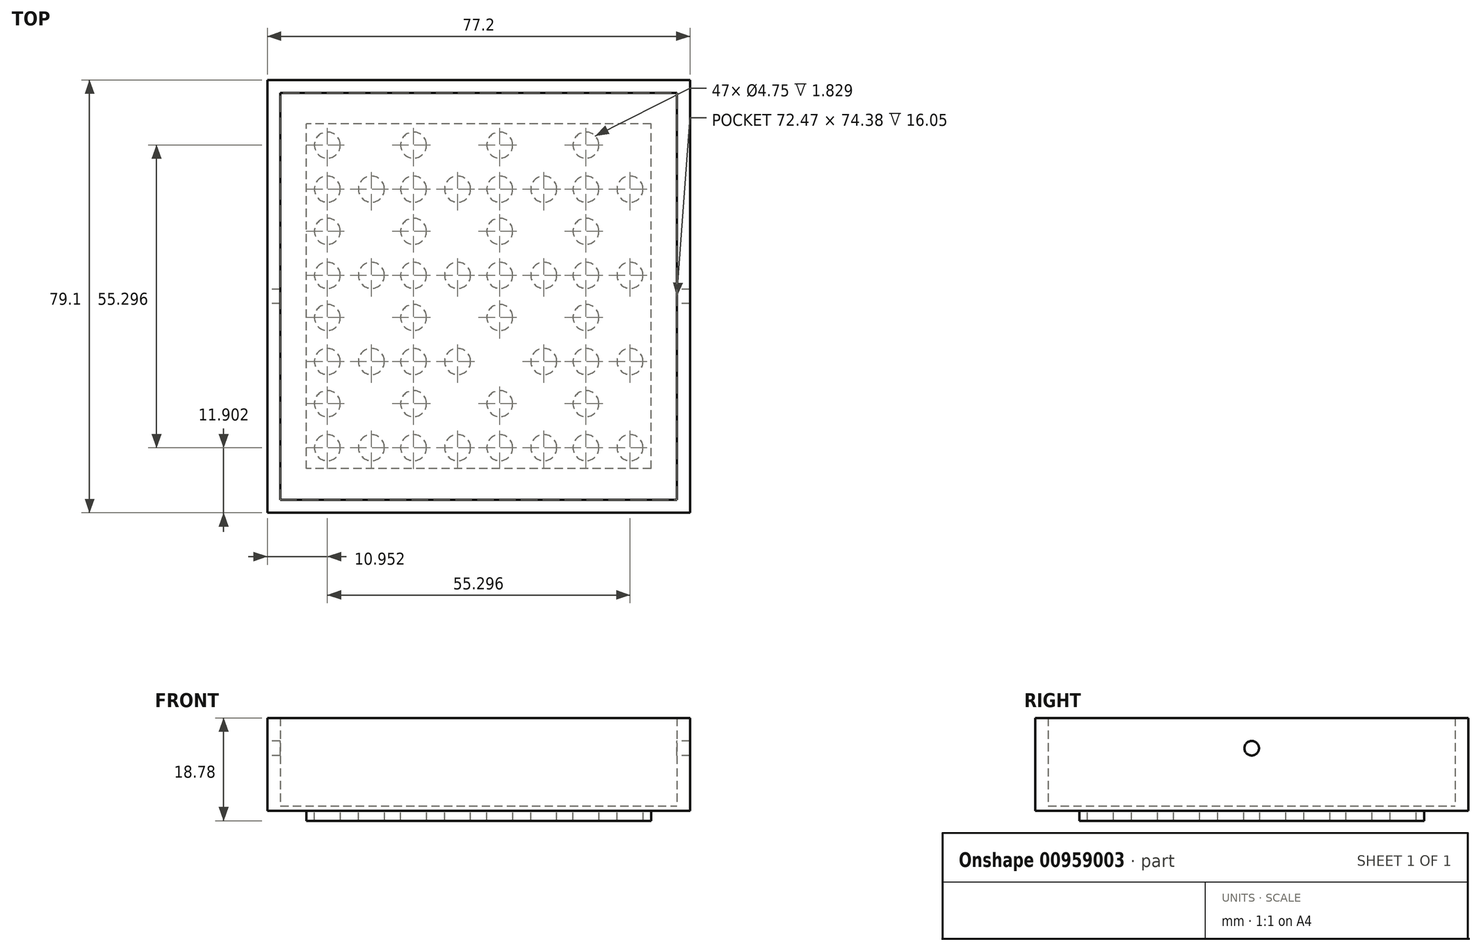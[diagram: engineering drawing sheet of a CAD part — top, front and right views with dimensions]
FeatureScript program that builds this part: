
annotation { "Feature Type Name" : "Feature", "Feature Type Description" : "" }
export const myFeature = defineFeature(function(context is Context, id is Id, definition is map)
    precondition{}
    {
        {
            var Q0;
            Q0=qCreatedBy(makeId("Top.planeOp"),FACE);
            var sketch = newSketch(context, id + "F0", { "sketchPlane" : qUnion([Q0])});
            skLineSegment(sketch, "E0.bottom", {"start": v(36.24, 37.19) * mm, "end": v(-36.24, 37.19) * mm});
            skLineSegment(sketch, "E0.top", {"start": v(36.24, -37.19) * mm, "end": v(-36.24, -37.19) * mm});
            skLineSegment(sketch, "E0.left", {"start": v(36.24, 37.19) * mm, "end": v(36.24, -37.19) * mm});
            skLineSegment(sketch, "E0.right", {"start": v(-36.24, 37.19) * mm, "end": v(-36.24, -37.19) * mm});
            skPoint(sketch, "E0.middle", {"position": v(0, 0) * mm});
            skLineSegment(sketch, "E1.bottom", {"start": v(-38.6, 39.55) * mm, "end": v(38.6, 39.55) * mm});
            skLineSegment(sketch, "E1.top", {"start": v(-38.6, -39.55) * mm, "end": v(38.6, -39.55) * mm});
            skLineSegment(sketch, "E1.left", {"start": v(-38.6, 39.55) * mm, "end": v(-38.6, -39.55) * mm});
            skLineSegment(sketch, "E1.right", {"start": v(38.6, 39.55) * mm, "end": v(38.6, -39.55) * mm});
            skSolve(sketch);
        }
        {
            var Q0;
            Q0=makeQuery(id+"F0.imprint","IMPRINT",FACE,{"disambiguationData":[TD([[makeQuery(id+"F0.imprint","IMPRINT",EDGE,{"derivedFrom":sQuery(id+"F0.wireOp",EDGE,"E0.bottom")}),-1.0]])]});
            extrude(context, id + "F1", {"entities" : qUnion([Q0]), "depth" : 16.95 * mm, "offsetDistance" : 25.4 * mm});
        }
        {
            var Q0;
            Q0=makeQuery(id+"F1.opExtrude","SWEPT_FACE",FACE,{"disambiguationData":[OSD([sQuery(id+"F0.wireOp",EDGE,"E1.left")])]});
            var sketch = newSketch(context, id + "F2", { "sketchPlane" : qUnion([Q0])});
            skLineSegment(sketch, "E2", {"start": v(-39.55, 0.9) * mm, "end": v(39.55, 0.9) * mm});
            skSolve(sketch);
        }
        {
            var Q0;
            {var subQ0=sQuery(id+"F2.wireOp",EDGE,"E2");Q0=makeQuery(id+"F2.imprint","IMPRINT",FACE,{"disambiguationData":[TD([[makeQuery(id+"F2.imprint","IMPRINT",EDGE,{"derivedFrom":subQ0}),-1.0]])]});}
            var Q1;
            Q1=makeQuery(id+"F1.opExtrude","SWEPT_FACE",FACE,{"disambiguationData":[OSD([sQuery(id+"F0.wireOp",EDGE,"E0.left")])]});
            extrude(context, id + "F3", {"entities" : qUnion([Q0]), "operationType" : NewBodyOperationType.ADD, "endBound" : BoundingType.UP_TO_SURFACE, "oppositeDirection" : true, "depth" : 25.4 * mm, "endBoundEntityFace" : qUnion([Q1]), "offsetDistance" : 25.4 * mm});
        }
        {
            var Q0;
            Q0=makeQuery(id+"F1.opExtrude","SWEPT_FACE",FACE,{"disambiguationData":[OSD([sQuery(id+"F0.wireOp",EDGE,"E1.left")])]});
            var sketch = newSketch(context, id + "F4", { "sketchPlane" : qUnion([Q0])});
            skLineSegment(sketch, "E3", {"start": v(39.55, 5.9) * mm, "end": v(-39.55, 5.9) * mm, "construction": true});
            skLineSegment(sketch, "E4", {"start": v(-39.55, 11.42) * mm, "end": v(39.55, 11.42) * mm, "construction": true});
            skCircle(sketch, "E5", {"center": v(0, 11.42) * mm, "radius": 1.33 * mm});
            skSolve(sketch);
        }
        {
            var Q0;
            Q0=makeQuery(id+"F4.imprint","IMPRINT",FACE,{"disambiguationData":[TD([[makeQuery(id+"F4.imprint","IMPRINT",EDGE,{"derivedFrom":sQuery(id+"F4.wireOp",EDGE,"E5")}),1.0]])]});
            extrude(context, id + "F5", {"entities" : qUnion([Q0]), "operationType" : NewBodyOperationType.REMOVE, "endBound" : BoundingType.THROUGH_ALL, "oppositeDirection" : true, "depth" : 25.4 * mm, "offsetDistance" : 25.4 * mm});
        }
        {
            var Q0;
            {var subQ0=sQuery(id+"F0.wireOp",EDGE,"E1.left");Q0=makeQuery(id+"F3.boolean.opBoolean","MERGE",FACE,{"derivedFrom":[makeQuery(id+"F1.opExtrude","CAP_FACE",FACE,{"disambiguationData":[OSD([sQuery(id+"F0.wireOp",EDGE,"E0.bottom"),sQuery(id+"F0.wireOp",EDGE,"E0.top"),sQuery(id+"F0.wireOp",EDGE,"E0.left"),sQuery(id+"F0.wireOp",EDGE,"E0.right"),sQuery(id+"F0.wireOp",EDGE,"E1.bottom"),sQuery(id+"F0.wireOp",EDGE,"E1.top"),subQ0,sQuery(id+"F0.wireOp",EDGE,"E1.right")])],"isStart":true}),makeQuery(id+"F3.opExtrude","SWEPT_FACE",FACE,{"disambiguationData":[OSD([subQ0])]})]});}
            var sketch = newSketch(context, id + "F6", { "sketchPlane" : qUnion([Q0])});
            skLineSegment(sketch, "E6.bottom", {"start": v(15.75, 15.75) * mm, "end": v(0, 15.75) * mm});
            skLineSegment(sketch, "E6.top", {"start": v(15.75, 0) * mm, "end": v(0, 0) * mm});
            skLineSegment(sketch, "E6.left", {"start": v(15.75, 15.75) * mm, "end": v(15.75, 0) * mm});
            skLineSegment(sketch, "E6.right", {"start": v(0, 15.75) * mm, "end": v(0, 0) * mm});
            skPoint(sketch, "E6.middle", {"position": v(7.87, 7.87) * mm});
            skLineSegment(sketch, "E7.bottom", {"start": v(14.27, 14.27) * mm, "end": v(1.47, 14.27) * mm, "construction": true});
            skLineSegment(sketch, "E7.top", {"start": v(14.27, 1.47) * mm, "end": v(1.47, 1.47) * mm, "construction": true});
            skLineSegment(sketch, "E7.left", {"start": v(14.27, 14.27) * mm, "end": v(14.27, 1.47) * mm, "construction": true});
            skLineSegment(sketch, "E7.right", {"start": v(1.47, 14.27) * mm, "end": v(1.47, 1.47) * mm, "construction": true});
            skCircle(sketch, "E8", {"center": v(3.85, 11.9) * mm, "radius": 2.37 * mm});
            skLineSegment(sketch, "E9", {"start": v(7.87, 14.27) * mm, "end": v(7.87, 1.47) * mm, "construction": true});
            skLineSegment(sketch, "E10", {"start": v(1.47, 7.87) * mm, "end": v(14.27, 7.87) * mm, "construction": true});
            skLineSegment(sketch, "E11.MirrorCS", {"start": v(14.27, 7.87) * mm, "end": v(1.47, 7.87) * mm, "construction": true});
            skCircle(sketch, "E12.MirrorC", {"center": v(11.9, 11.9) * mm, "radius": 2.37 * mm});
            skCircle(sketch, "E13.MirrorC", {"center": v(3.85, 3.85) * mm, "radius": 2.37 * mm});
            skCircle(sketch, "E14.MirrorC", {"center": v(11.9, 3.85) * mm, "radius": 2.37 * mm});
            skLineSegment(sketch, "E15.0.1.1", {"start": v(14.27, 30.02) * mm, "end": v(14.27, 17.22) * mm, "construction": true});
            skLineSegment(sketch, "E15.0.1.2", {"start": v(7.87, 30.02) * mm, "end": v(7.87, 17.22) * mm, "construction": true});
            skCircle(sketch, "E15.0.1.3", {"center": v(11.9, 19.6) * mm, "radius": 2.37 * mm});
            skCircle(sketch, "E15.0.1.4", {"center": v(3.85, 27.65) * mm, "radius": 2.37 * mm});
            skCircle(sketch, "E15.0.1.5", {"center": v(3.85, 19.6) * mm, "radius": 2.37 * mm});
            skLineSegment(sketch, "E15.0.1.6", {"start": v(1.47, 23.62) * mm, "end": v(14.27, 23.62) * mm, "construction": true});
            skLineSegment(sketch, "E15.0.1.7", {"start": v(14.27, 30.02) * mm, "end": v(1.47, 30.02) * mm, "construction": true});
            skCircle(sketch, "E15.0.1.8", {"center": v(11.9, 27.65) * mm, "radius": 2.37 * mm});
            skLineSegment(sketch, "E15.0.1.9", {"start": v(14.27, 17.22) * mm, "end": v(1.47, 17.22) * mm, "construction": true});
            skPoint(sketch, "E15.0.1.10", {"position": v(7.87, 23.62) * mm});
            skLineSegment(sketch, "E15.0.1.11", {"start": v(15.75, 31.5) * mm, "end": v(15.75, 15.75) * mm});
            skLineSegment(sketch, "E15.0.1.12", {"start": v(15.75, 31.5) * mm, "end": v(0, 31.5) * mm});
            skLineSegment(sketch, "E15.0.1.13", {"start": v(0, 31.5) * mm, "end": v(0, 15.75) * mm});
            skLineSegment(sketch, "E15.0.1.14", {"start": v(1.47, 30.02) * mm, "end": v(1.47, 17.22) * mm, "construction": true});
            skPoint(sketch, "E15.0.1.15", {"position": v(7.87, 23.62) * mm});
            skLineSegment(sketch, "E15.0.1.16", {"start": v(14.27, 23.62) * mm, "end": v(1.47, 23.62) * mm, "construction": true});
            skCircle(sketch, "E15.0.1.17", {"center": v(3.85, 27.65) * mm, "radius": 2.37 * mm});
            skLineSegment(sketch, "E15.0.1.18", {"start": v(1.47, 23.62) * mm, "end": v(14.27, 23.62) * mm, "construction": true});
            skLineSegment(sketch, "E15.1.0.0", {"start": v(31.5, 0) * mm, "end": v(15.75, 0) * mm});
            skLineSegment(sketch, "E15.1.0.1", {"start": v(30.02, 14.27) * mm, "end": v(30.02, 1.47) * mm, "construction": true});
            skLineSegment(sketch, "E15.1.0.2", {"start": v(23.62, 14.27) * mm, "end": v(23.62, 1.47) * mm, "construction": true});
            skCircle(sketch, "E15.1.0.3", {"center": v(27.65, 3.85) * mm, "radius": 2.37 * mm});
            skCircle(sketch, "E15.1.0.4", {"center": v(19.6, 11.9) * mm, "radius": 2.37 * mm});
            skCircle(sketch, "E15.1.0.5", {"center": v(19.6, 3.85) * mm, "radius": 2.37 * mm});
            skLineSegment(sketch, "E15.1.0.6", {"start": v(17.22, 7.87) * mm, "end": v(30.02, 7.87) * mm, "construction": true});
            skLineSegment(sketch, "E15.1.0.7", {"start": v(30.02, 14.27) * mm, "end": v(17.22, 14.27) * mm, "construction": true});
            skCircle(sketch, "E15.1.0.8", {"center": v(27.65, 11.9) * mm, "radius": 2.37 * mm});
            skLineSegment(sketch, "E15.1.0.9", {"start": v(30.02, 1.47) * mm, "end": v(17.22, 1.47) * mm, "construction": true});
            skPoint(sketch, "E15.1.0.10", {"position": v(23.62, 7.87) * mm});
            skLineSegment(sketch, "E15.1.0.11", {"start": v(31.5, 15.75) * mm, "end": v(31.5, 0) * mm});
            skLineSegment(sketch, "E15.1.0.12", {"start": v(31.5, 15.75) * mm, "end": v(15.75, 15.75) * mm});
            skLineSegment(sketch, "E15.1.0.14", {"start": v(17.22, 14.27) * mm, "end": v(17.22, 1.47) * mm, "construction": true});
            skPoint(sketch, "E15.1.0.15", {"position": v(23.62, 7.87) * mm});
            skLineSegment(sketch, "E15.1.0.16", {"start": v(30.02, 7.87) * mm, "end": v(17.22, 7.87) * mm, "construction": true});
            skCircle(sketch, "E15.1.0.17", {"center": v(19.6, 11.9) * mm, "radius": 2.37 * mm});
            skLineSegment(sketch, "E15.1.0.18", {"start": v(17.22, 7.87) * mm, "end": v(30.02, 7.87) * mm, "construction": true});
            skLineSegment(sketch, "E15.1.1.0", {"start": v(31.5, 15.75) * mm, "end": v(15.75, 15.75) * mm});
            skLineSegment(sketch, "E15.1.1.1", {"start": v(30.02, 30.02) * mm, "end": v(30.02, 17.22) * mm, "construction": true});
            skLineSegment(sketch, "E15.1.1.2", {"start": v(23.62, 30.02) * mm, "end": v(23.62, 17.22) * mm, "construction": true});
            skCircle(sketch, "E15.1.1.3", {"center": v(27.65, 19.6) * mm, "radius": 2.37 * mm});
            skCircle(sketch, "E15.1.1.4", {"center": v(19.6, 27.65) * mm, "radius": 2.37 * mm});
            skCircle(sketch, "E15.1.1.5", {"center": v(19.6, 19.6) * mm, "radius": 2.37 * mm});
            skLineSegment(sketch, "E15.1.1.6", {"start": v(17.22, 23.62) * mm, "end": v(30.02, 23.62) * mm, "construction": true});
            skLineSegment(sketch, "E15.1.1.7", {"start": v(30.02, 30.02) * mm, "end": v(17.22, 30.02) * mm, "construction": true});
            skCircle(sketch, "E15.1.1.8", {"center": v(27.65, 27.65) * mm, "radius": 2.37 * mm});
            skLineSegment(sketch, "E15.1.1.9", {"start": v(30.02, 17.22) * mm, "end": v(17.22, 17.22) * mm, "construction": true});
            skPoint(sketch, "E15.1.1.10", {"position": v(23.62, 23.62) * mm});
            skLineSegment(sketch, "E15.1.1.11", {"start": v(31.5, 31.5) * mm, "end": v(31.5, 15.75) * mm});
            skLineSegment(sketch, "E15.1.1.12", {"start": v(31.5, 31.5) * mm, "end": v(15.75, 31.5) * mm});
            skLineSegment(sketch, "E15.1.1.13", {"start": v(15.75, 31.5) * mm, "end": v(15.75, 15.75) * mm});
            skLineSegment(sketch, "E15.1.1.14", {"start": v(17.22, 30.02) * mm, "end": v(17.22, 17.22) * mm, "construction": true});
            skPoint(sketch, "E15.1.1.15", {"position": v(23.62, 23.62) * mm});
            skLineSegment(sketch, "E15.1.1.16", {"start": v(30.02, 23.62) * mm, "end": v(17.22, 23.62) * mm, "construction": true});
            skCircle(sketch, "E15.1.1.17", {"center": v(19.6, 27.65) * mm, "radius": 2.37 * mm});
            skLineSegment(sketch, "E15.1.1.18", {"start": v(17.22, 23.62) * mm, "end": v(30.02, 23.62) * mm, "construction": true});
            skLineSegment(sketch, "E15.direction1", {"start": v(0, 0) * mm, "end": v(15.75, 0) * mm, "construction": true});
            skLineSegment(sketch, "E15.direction2", {"start": v(0, 0) * mm, "end": v(0, 15.75) * mm, "construction": true});
            skPoint(sketch, "E16.0.1.0", {"position": v(23.62, -7.87) * mm});
            skLineSegment(sketch, "E16.0.1.1", {"start": v(1.47, -17.22) * mm, "end": v(1.47, -30.02) * mm, "construction": true});
            skLineSegment(sketch, "E16.0.1.3", {"start": v(14.27, -17.22) * mm, "end": v(14.27, -30.02) * mm, "construction": true});
            skLineSegment(sketch, "E16.0.1.4", {"start": v(17.22, -23.62) * mm, "end": v(30.02, -23.62) * mm, "construction": true});
            skLineSegment(sketch, "E16.0.1.5", {"start": v(31.5, -15.75) * mm, "end": v(15.75, -15.75) * mm});
            skLineSegment(sketch, "E16.0.1.6", {"start": v(17.22, -7.87) * mm, "end": v(30.02, -7.87) * mm, "construction": true});
            skCircle(sketch, "E16.0.1.7", {"center": v(11.9, -19.6) * mm, "radius": 2.37 * mm});
            skCircle(sketch, "E16.0.1.8", {"center": v(27.65, -19.6) * mm, "radius": 2.37 * mm});
            skCircle(sketch, "E16.0.1.9", {"center": v(19.6, -11.9) * mm, "radius": 2.37 * mm});
            skLineSegment(sketch, "E16.0.1.10", {"start": v(1.47, -1.47) * mm, "end": v(1.47, -14.27) * mm, "construction": true});
            skLineSegment(sketch, "E16.0.1.11", {"start": v(30.02, -1.47) * mm, "end": v(30.02, -14.27) * mm, "construction": true});
            skLineSegment(sketch, "E16.0.1.12", {"start": v(31.5, -15.75) * mm, "end": v(31.5, -31.5) * mm});
            skCircle(sketch, "E16.0.1.13", {"center": v(3.85, -27.65) * mm, "radius": 2.37 * mm});
            skLineSegment(sketch, "E16.0.1.14", {"start": v(14.27, -30.02) * mm, "end": v(1.47, -30.02) * mm, "construction": true});
            skCircle(sketch, "E16.0.1.15", {"center": v(19.6, -3.85) * mm, "radius": 2.37 * mm});
            skCircle(sketch, "E16.0.1.16", {"center": v(19.6, -27.65) * mm, "radius": 2.37 * mm});
            skLineSegment(sketch, "E16.0.1.17", {"start": v(14.27, -17.22) * mm, "end": v(1.47, -17.22) * mm, "construction": true});
            skLineSegment(sketch, "E16.0.1.18", {"start": v(15.75, -15.75) * mm, "end": v(15.75, -31.5) * mm});
            skLineSegment(sketch, "E16.0.1.19", {"start": v(31.5, -31.5) * mm, "end": v(15.75, -31.5) * mm});
            skLineSegment(sketch, "E16.0.1.20", {"start": v(15.75, -15.75) * mm, "end": v(0, -15.75) * mm});
            skLineSegment(sketch, "E16.0.1.21", {"start": v(30.02, -1.47) * mm, "end": v(17.22, -1.47) * mm, "construction": true});
            skCircle(sketch, "E16.0.1.22", {"center": v(11.9, -3.85) * mm, "radius": 2.37 * mm});
            skLineSegment(sketch, "E16.0.1.23", {"start": v(23.62, -17.22) * mm, "end": v(23.62, -30.02) * mm, "construction": true});
            skLineSegment(sketch, "E16.0.1.24", {"start": v(31.5, 0) * mm, "end": v(31.5, -15.75) * mm});
            skCircle(sketch, "E16.0.1.25", {"center": v(27.65, -27.65) * mm, "radius": 2.37 * mm});
            skLineSegment(sketch, "E16.0.1.26", {"start": v(7.87, -1.47) * mm, "end": v(7.87, -14.27) * mm, "construction": true});
            skLineSegment(sketch, "E16.0.1.27", {"start": v(30.02, -17.22) * mm, "end": v(17.22, -17.22) * mm, "construction": true});
            skLineSegment(sketch, "E16.0.1.28", {"start": v(14.27, -1.47) * mm, "end": v(14.27, -14.27) * mm, "construction": true});
            skLineSegment(sketch, "E16.0.1.29", {"start": v(15.75, 0) * mm, "end": v(15.75, -15.75) * mm});
            skLineSegment(sketch, "E16.0.1.30", {"start": v(1.47, -7.87) * mm, "end": v(14.27, -7.87) * mm, "construction": true});
            skPoint(sketch, "E16.0.1.31", {"position": v(7.87, -7.87) * mm});
            skLineSegment(sketch, "E16.0.1.32", {"start": v(14.27, -14.27) * mm, "end": v(1.47, -14.27) * mm, "construction": true});
            skLineSegment(sketch, "E16.0.1.33", {"start": v(17.22, -17.22) * mm, "end": v(17.22, -30.02) * mm, "construction": true});
            skLineSegment(sketch, "E16.0.1.34", {"start": v(0, -31.5) * mm, "end": v(0, -15.75) * mm, "construction": true});
            skCircle(sketch, "E16.0.1.35", {"center": v(27.65, -11.9) * mm, "radius": 2.37 * mm});
            skCircle(sketch, "E16.0.1.36", {"center": v(11.9, -11.9) * mm, "radius": 2.37 * mm});
            skPoint(sketch, "E16.0.1.37", {"position": v(7.87, -23.62) * mm});
            skCircle(sketch, "E16.0.1.38", {"center": v(3.85, -19.6) * mm, "radius": 2.37 * mm});
            skLineSegment(sketch, "E16.0.1.39", {"start": v(0, 0) * mm, "end": v(0, -15.75) * mm});
            skLineSegment(sketch, "E16.0.1.40", {"start": v(30.02, -30.02) * mm, "end": v(17.22, -30.02) * mm, "construction": true});
            skLineSegment(sketch, "E16.0.1.41", {"start": v(17.22, -1.47) * mm, "end": v(17.22, -14.27) * mm, "construction": true});
            skCircle(sketch, "E16.0.1.42", {"center": v(27.65, -3.85) * mm, "radius": 2.37 * mm});
            skCircle(sketch, "E16.0.1.43", {"center": v(19.6, -19.6) * mm, "radius": 2.37 * mm});
            skCircle(sketch, "E16.0.1.44", {"center": v(3.85, -11.9) * mm, "radius": 2.37 * mm});
            skPoint(sketch, "E16.0.1.45", {"position": v(23.62, -23.62) * mm});
            skLineSegment(sketch, "E16.0.1.46", {"start": v(30.02, -14.27) * mm, "end": v(17.22, -14.27) * mm, "construction": true});
            skLineSegment(sketch, "E16.0.1.47", {"start": v(0, -31.5) * mm, "end": v(15.75, -31.5) * mm, "construction": true});
            skCircle(sketch, "E16.0.1.48", {"center": v(3.85, -3.85) * mm, "radius": 2.37 * mm});
            skLineSegment(sketch, "E16.0.1.49", {"start": v(14.27, -1.47) * mm, "end": v(1.47, -1.47) * mm, "construction": true});
            skLineSegment(sketch, "E16.0.1.50", {"start": v(30.02, -17.22) * mm, "end": v(30.02, -30.02) * mm, "construction": true});
            skCircle(sketch, "E16.0.1.51", {"center": v(11.9, -27.65) * mm, "radius": 2.37 * mm});
            skLineSegment(sketch, "E16.0.1.52", {"start": v(1.47, -23.62) * mm, "end": v(14.27, -23.62) * mm, "construction": true});
            skLineSegment(sketch, "E16.0.1.53", {"start": v(23.62, -1.47) * mm, "end": v(23.62, -14.27) * mm, "construction": true});
            skLineSegment(sketch, "E16.0.1.55", {"start": v(7.87, -17.22) * mm, "end": v(7.87, -30.02) * mm, "construction": true});
            skLineSegment(sketch, "E16.0.1.56", {"start": v(30.02, -7.87) * mm, "end": v(17.22, -7.87) * mm, "construction": true});
            skLineSegment(sketch, "E16.0.1.57", {"start": v(0, -15.75) * mm, "end": v(0, -31.5) * mm});
            skLineSegment(sketch, "E16.0.1.58", {"start": v(15.75, -31.5) * mm, "end": v(0, -31.5) * mm});
            skLineSegment(sketch, "E16.0.1.59", {"start": v(1.47, -7.87) * mm, "end": v(14.27, -7.87) * mm, "construction": true});
            skLineSegment(sketch, "E16.0.1.60", {"start": v(15.75, 0) * mm, "end": v(15.75, -15.75) * mm});
            skLineSegment(sketch, "E16.0.1.61", {"start": v(30.02, -23.62) * mm, "end": v(17.22, -23.62) * mm, "construction": true});
            skCircle(sketch, "E16.0.1.62", {"center": v(19.6, -3.85) * mm, "radius": 2.37 * mm});
            skLineSegment(sketch, "E16.0.1.63", {"start": v(31.5, -15.75) * mm, "end": v(15.75, -15.75) * mm});
            skCircle(sketch, "E16.0.1.64", {"center": v(3.85, -19.6) * mm, "radius": 2.37 * mm});
            skPoint(sketch, "E16.0.1.65", {"position": v(23.62, -23.62) * mm});
            skLineSegment(sketch, "E16.0.1.66", {"start": v(15.75, -15.75) * mm, "end": v(15.75, -31.5) * mm});
            skPoint(sketch, "E16.0.1.67", {"position": v(7.87, -23.62) * mm});
            skLineSegment(sketch, "E16.0.1.68", {"start": v(14.27, -23.62) * mm, "end": v(1.47, -23.62) * mm, "construction": true});
            skPoint(sketch, "E16.0.1.69", {"position": v(23.62, -7.87) * mm});
            skCircle(sketch, "E16.0.1.70", {"center": v(19.6, -19.6) * mm, "radius": 2.37 * mm});
            skPoint(sketch, "E16.0.1.71", {"position": v(7.87, -7.87) * mm});
            skLineSegment(sketch, "E16.0.1.72", {"start": v(15.75, -15.75) * mm, "end": v(0, -15.75) * mm});
            skCircle(sketch, "E16.0.1.73", {"center": v(3.85, -3.85) * mm, "radius": 2.37 * mm});
            skLineSegment(sketch, "E16.0.1.74", {"start": v(17.22, -7.87) * mm, "end": v(30.02, -7.87) * mm, "construction": true});
            skLineSegment(sketch, "E16.0.1.75", {"start": v(17.22, -23.62) * mm, "end": v(30.02, -23.62) * mm, "construction": true});
            skLineSegment(sketch, "E16.0.1.76", {"start": v(1.47, -23.62) * mm, "end": v(14.27, -23.62) * mm, "construction": true});
            skLineSegment(sketch, "E16.0.1.77", {"start": v(14.27, -7.87) * mm, "end": v(1.47, -7.87) * mm, "construction": true});
            skPoint(sketch, "E16.1.0.0", {"position": v(-7.87, 23.62) * mm});
            skLineSegment(sketch, "E16.1.0.1", {"start": v(-30.02, 14.27) * mm, "end": v(-30.02, 1.47) * mm, "construction": true});
            skLineSegment(sketch, "E16.1.0.2", {"start": v(-15.75, 31.5) * mm, "end": v(-31.5, 31.5) * mm});
            skLineSegment(sketch, "E16.1.0.3", {"start": v(-17.22, 14.27) * mm, "end": v(-17.22, 1.47) * mm, "construction": true});
            skLineSegment(sketch, "E16.1.0.4", {"start": v(-14.27, 7.87) * mm, "end": v(-1.47, 7.87) * mm, "construction": true});
            skLineSegment(sketch, "E16.1.0.5", {"start": v(0, 15.75) * mm, "end": v(-15.75, 15.75) * mm});
            skLineSegment(sketch, "E16.1.0.6", {"start": v(-14.27, 23.62) * mm, "end": v(-1.47, 23.62) * mm, "construction": true});
            skCircle(sketch, "E16.1.0.7", {"center": v(-19.6, 11.9) * mm, "radius": 2.37 * mm});
            skCircle(sketch, "E16.1.0.8", {"center": v(-3.85, 11.9) * mm, "radius": 2.37 * mm});
            skCircle(sketch, "E16.1.0.9", {"center": v(-11.9, 19.6) * mm, "radius": 2.37 * mm});
            skLineSegment(sketch, "E16.1.0.10", {"start": v(-30.02, 30.02) * mm, "end": v(-30.02, 17.22) * mm, "construction": true});
            skLineSegment(sketch, "E16.1.0.11", {"start": v(-1.47, 30.02) * mm, "end": v(-1.47, 17.22) * mm, "construction": true});
            skCircle(sketch, "E16.1.0.13", {"center": v(-27.65, 3.85) * mm, "radius": 2.37 * mm});
            skLineSegment(sketch, "E16.1.0.14", {"start": v(-17.22, 1.47) * mm, "end": v(-30.02, 1.47) * mm, "construction": true});
            skCircle(sketch, "E16.1.0.15", {"center": v(-11.9, 27.65) * mm, "radius": 2.37 * mm});
            skCircle(sketch, "E16.1.0.16", {"center": v(-11.9, 3.85) * mm, "radius": 2.37 * mm});
            skLineSegment(sketch, "E16.1.0.17", {"start": v(-17.22, 14.27) * mm, "end": v(-30.02, 14.27) * mm, "construction": true});
            skLineSegment(sketch, "E16.1.0.18", {"start": v(-15.75, 15.75) * mm, "end": v(-15.75, 0) * mm});
            skLineSegment(sketch, "E16.1.0.19", {"start": v(0, 0) * mm, "end": v(-15.75, 0) * mm});
            skLineSegment(sketch, "E16.1.0.20", {"start": v(-15.75, 15.75) * mm, "end": v(-31.5, 15.75) * mm});
            skLineSegment(sketch, "E16.1.0.21", {"start": v(-1.47, 30.02) * mm, "end": v(-14.27, 30.02) * mm, "construction": true});
            skCircle(sketch, "E16.1.0.22", {"center": v(-19.6, 27.65) * mm, "radius": 2.37 * mm});
            skLineSegment(sketch, "E16.1.0.23", {"start": v(-7.87, 14.27) * mm, "end": v(-7.87, 1.47) * mm, "construction": true});
            skCircle(sketch, "E16.1.0.25", {"center": v(-3.85, 3.85) * mm, "radius": 2.37 * mm});
            skLineSegment(sketch, "E16.1.0.26", {"start": v(-23.62, 30.02) * mm, "end": v(-23.62, 17.22) * mm, "construction": true});
            skLineSegment(sketch, "E16.1.0.27", {"start": v(-1.47, 14.27) * mm, "end": v(-14.27, 14.27) * mm, "construction": true});
            skLineSegment(sketch, "E16.1.0.28", {"start": v(-17.22, 30.02) * mm, "end": v(-17.22, 17.22) * mm, "construction": true});
            skLineSegment(sketch, "E16.1.0.29", {"start": v(-15.75, 31.5) * mm, "end": v(-15.75, 15.75) * mm});
            skLineSegment(sketch, "E16.1.0.30", {"start": v(-30.02, 23.62) * mm, "end": v(-17.22, 23.62) * mm, "construction": true});
            skPoint(sketch, "E16.1.0.31", {"position": v(-23.62, 23.62) * mm});
            skLineSegment(sketch, "E16.1.0.32", {"start": v(-17.22, 17.22) * mm, "end": v(-30.02, 17.22) * mm, "construction": true});
            skLineSegment(sketch, "E16.1.0.33", {"start": v(-14.27, 14.27) * mm, "end": v(-14.27, 1.47) * mm, "construction": true});
            skLineSegment(sketch, "E16.1.0.34", {"start": v(-31.5, 0) * mm, "end": v(-31.5, 15.75) * mm, "construction": true});
            skCircle(sketch, "E16.1.0.35", {"center": v(-3.85, 19.6) * mm, "radius": 2.37 * mm});
            skCircle(sketch, "E16.1.0.36", {"center": v(-19.6, 19.6) * mm, "radius": 2.37 * mm});
            skPoint(sketch, "E16.1.0.37", {"position": v(-23.62, 7.87) * mm});
            skCircle(sketch, "E16.1.0.38", {"center": v(-27.65, 11.9) * mm, "radius": 2.37 * mm});
            skLineSegment(sketch, "E16.1.0.39", {"start": v(-31.5, 31.5) * mm, "end": v(-31.5, 15.75) * mm});
            skLineSegment(sketch, "E16.1.0.40", {"start": v(-1.47, 1.47) * mm, "end": v(-14.27, 1.47) * mm, "construction": true});
            skLineSegment(sketch, "E16.1.0.41", {"start": v(-14.27, 30.02) * mm, "end": v(-14.27, 17.22) * mm, "construction": true});
            skCircle(sketch, "E16.1.0.42", {"center": v(-3.85, 27.65) * mm, "radius": 2.37 * mm});
            skCircle(sketch, "E16.1.0.43", {"center": v(-11.9, 11.9) * mm, "radius": 2.37 * mm});
            skCircle(sketch, "E16.1.0.44", {"center": v(-27.65, 19.6) * mm, "radius": 2.37 * mm});
            skPoint(sketch, "E16.1.0.45", {"position": v(-7.87, 7.87) * mm});
            skLineSegment(sketch, "E16.1.0.46", {"start": v(-1.47, 17.22) * mm, "end": v(-14.27, 17.22) * mm, "construction": true});
            skLineSegment(sketch, "E16.1.0.47", {"start": v(-31.5, 0) * mm, "end": v(-15.75, 0) * mm, "construction": true});
            skCircle(sketch, "E16.1.0.48", {"center": v(-27.65, 27.65) * mm, "radius": 2.37 * mm});
            skLineSegment(sketch, "E16.1.0.49", {"start": v(-17.22, 30.02) * mm, "end": v(-30.02, 30.02) * mm, "construction": true});
            skLineSegment(sketch, "E16.1.0.50", {"start": v(-1.47, 14.27) * mm, "end": v(-1.47, 1.47) * mm, "construction": true});
            skCircle(sketch, "E16.1.0.51", {"center": v(-19.6, 3.85) * mm, "radius": 2.37 * mm});
            skLineSegment(sketch, "E16.1.0.52", {"start": v(-30.02, 7.87) * mm, "end": v(-17.22, 7.87) * mm, "construction": true});
            skLineSegment(sketch, "E16.1.0.53", {"start": v(-7.87, 30.02) * mm, "end": v(-7.87, 17.22) * mm, "construction": true});
            skLineSegment(sketch, "E16.1.0.54", {"start": v(0, 31.5) * mm, "end": v(-15.75, 31.5) * mm});
            skLineSegment(sketch, "E16.1.0.55", {"start": v(-23.62, 14.27) * mm, "end": v(-23.62, 1.47) * mm, "construction": true});
            skLineSegment(sketch, "E16.1.0.56", {"start": v(-1.47, 23.62) * mm, "end": v(-14.27, 23.62) * mm, "construction": true});
            skLineSegment(sketch, "E16.1.0.57", {"start": v(-31.5, 15.75) * mm, "end": v(-31.5, 0) * mm});
            skLineSegment(sketch, "E16.1.0.58", {"start": v(-15.75, 0) * mm, "end": v(-31.5, 0) * mm});
            skLineSegment(sketch, "E16.1.0.59", {"start": v(-30.02, 23.62) * mm, "end": v(-17.22, 23.62) * mm, "construction": true});
            skLineSegment(sketch, "E16.1.0.60", {"start": v(-15.75, 31.5) * mm, "end": v(-15.75, 15.75) * mm});
            skLineSegment(sketch, "E16.1.0.61", {"start": v(-1.47, 7.87) * mm, "end": v(-14.27, 7.87) * mm, "construction": true});
            skCircle(sketch, "E16.1.0.62", {"center": v(-11.9, 27.65) * mm, "radius": 2.37 * mm});
            skLineSegment(sketch, "E16.1.0.63", {"start": v(0, 15.75) * mm, "end": v(-15.75, 15.75) * mm});
            skCircle(sketch, "E16.1.0.64", {"center": v(-27.65, 11.9) * mm, "radius": 2.37 * mm});
            skPoint(sketch, "E16.1.0.65", {"position": v(-7.87, 7.87) * mm});
            skLineSegment(sketch, "E16.1.0.66", {"start": v(-15.75, 15.75) * mm, "end": v(-15.75, 0) * mm});
            skPoint(sketch, "E16.1.0.67", {"position": v(-23.62, 7.87) * mm});
            skLineSegment(sketch, "E16.1.0.68", {"start": v(-17.22, 7.87) * mm, "end": v(-30.02, 7.87) * mm, "construction": true});
            skPoint(sketch, "E16.1.0.69", {"position": v(-7.87, 23.62) * mm});
            skCircle(sketch, "E16.1.0.70", {"center": v(-11.9, 11.9) * mm, "radius": 2.37 * mm});
            skPoint(sketch, "E16.1.0.71", {"position": v(-23.62, 23.62) * mm});
            skLineSegment(sketch, "E16.1.0.72", {"start": v(-15.75, 15.75) * mm, "end": v(-31.5, 15.75) * mm});
            skCircle(sketch, "E16.1.0.73", {"center": v(-27.65, 27.65) * mm, "radius": 2.37 * mm});
            skLineSegment(sketch, "E16.1.0.74", {"start": v(-14.27, 23.62) * mm, "end": v(-1.47, 23.62) * mm, "construction": true});
            skLineSegment(sketch, "E16.1.0.75", {"start": v(-14.27, 7.87) * mm, "end": v(-1.47, 7.87) * mm, "construction": true});
            skLineSegment(sketch, "E16.1.0.76", {"start": v(-30.02, 7.87) * mm, "end": v(-17.22, 7.87) * mm, "construction": true});
            skLineSegment(sketch, "E16.1.0.77", {"start": v(-17.22, 23.62) * mm, "end": v(-30.02, 23.62) * mm, "construction": true});
            skPoint(sketch, "E16.1.1.0", {"position": v(-7.87, -7.87) * mm});
            skLineSegment(sketch, "E16.1.1.1", {"start": v(-30.02, -17.22) * mm, "end": v(-30.02, -30.02) * mm, "construction": true});
            skLineSegment(sketch, "E16.1.1.2", {"start": v(-15.75, 0) * mm, "end": v(-31.5, 0) * mm});
            skLineSegment(sketch, "E16.1.1.3", {"start": v(-17.22, -17.22) * mm, "end": v(-17.22, -30.02) * mm, "construction": true});
            skLineSegment(sketch, "E16.1.1.4", {"start": v(-14.27, -23.62) * mm, "end": v(-1.47, -23.62) * mm, "construction": true});
            skLineSegment(sketch, "E16.1.1.5", {"start": v(0, -15.75) * mm, "end": v(-15.75, -15.75) * mm});
            skLineSegment(sketch, "E16.1.1.6", {"start": v(-14.27, -7.87) * mm, "end": v(-1.47, -7.87) * mm, "construction": true});
            skCircle(sketch, "E16.1.1.7", {"center": v(-19.6, -19.6) * mm, "radius": 2.37 * mm});
            skCircle(sketch, "E16.1.1.8", {"center": v(-3.85, -19.6) * mm, "radius": 2.37 * mm});
            skCircle(sketch, "E16.1.1.9", {"center": v(-11.9, -11.9) * mm, "radius": 2.37 * mm});
            skLineSegment(sketch, "E16.1.1.10", {"start": v(-30.02, -1.47) * mm, "end": v(-30.02, -14.27) * mm, "construction": true});
            skLineSegment(sketch, "E16.1.1.11", {"start": v(-1.47, -1.47) * mm, "end": v(-1.47, -14.27) * mm, "construction": true});
            skLineSegment(sketch, "E16.1.1.12", {"start": v(0, -15.75) * mm, "end": v(0, -31.5) * mm});
            skCircle(sketch, "E16.1.1.13", {"center": v(-27.65, -27.65) * mm, "radius": 2.37 * mm});
            skLineSegment(sketch, "E16.1.1.14", {"start": v(-17.22, -30.02) * mm, "end": v(-30.02, -30.02) * mm, "construction": true});
            skCircle(sketch, "E16.1.1.15", {"center": v(-11.9, -3.85) * mm, "radius": 2.37 * mm});
            skCircle(sketch, "E16.1.1.16", {"center": v(-11.9, -27.65) * mm, "radius": 2.37 * mm});
            skLineSegment(sketch, "E16.1.1.17", {"start": v(-17.22, -17.22) * mm, "end": v(-30.02, -17.22) * mm, "construction": true});
            skLineSegment(sketch, "E16.1.1.18", {"start": v(-15.75, -15.75) * mm, "end": v(-15.75, -31.5) * mm});
            skLineSegment(sketch, "E16.1.1.19", {"start": v(0, -31.5) * mm, "end": v(-15.75, -31.5) * mm});
            skLineSegment(sketch, "E16.1.1.20", {"start": v(-15.75, -15.75) * mm, "end": v(-31.5, -15.75) * mm});
            skLineSegment(sketch, "E16.1.1.21", {"start": v(-1.47, -1.47) * mm, "end": v(-14.27, -1.47) * mm, "construction": true});
            skCircle(sketch, "E16.1.1.22", {"center": v(-19.6, -3.85) * mm, "radius": 2.37 * mm});
            skLineSegment(sketch, "E16.1.1.23", {"start": v(-7.87, -17.22) * mm, "end": v(-7.87, -30.02) * mm, "construction": true});
            skLineSegment(sketch, "E16.1.1.24", {"start": v(0, 0) * mm, "end": v(0, -15.75) * mm});
            skCircle(sketch, "E16.1.1.25", {"center": v(-3.85, -27.65) * mm, "radius": 2.37 * mm});
            skLineSegment(sketch, "E16.1.1.26", {"start": v(-23.62, -1.47) * mm, "end": v(-23.62, -14.27) * mm, "construction": true});
            skLineSegment(sketch, "E16.1.1.27", {"start": v(-1.47, -17.22) * mm, "end": v(-14.27, -17.22) * mm, "construction": true});
            skLineSegment(sketch, "E16.1.1.28", {"start": v(-17.22, -1.47) * mm, "end": v(-17.22, -14.27) * mm, "construction": true});
            skLineSegment(sketch, "E16.1.1.29", {"start": v(-15.75, 0) * mm, "end": v(-15.75, -15.75) * mm});
            skLineSegment(sketch, "E16.1.1.30", {"start": v(-30.02, -7.87) * mm, "end": v(-17.22, -7.87) * mm, "construction": true});
            skPoint(sketch, "E16.1.1.31", {"position": v(-23.62, -7.87) * mm});
            skLineSegment(sketch, "E16.1.1.32", {"start": v(-17.22, -14.27) * mm, "end": v(-30.02, -14.27) * mm, "construction": true});
            skLineSegment(sketch, "E16.1.1.33", {"start": v(-14.27, -17.22) * mm, "end": v(-14.27, -30.02) * mm, "construction": true});
            skLineSegment(sketch, "E16.1.1.34", {"start": v(-31.5, -31.5) * mm, "end": v(-31.5, -15.75) * mm, "construction": true});
            skCircle(sketch, "E16.1.1.35", {"center": v(-3.85, -11.9) * mm, "radius": 2.37 * mm});
            skCircle(sketch, "E16.1.1.36", {"center": v(-19.6, -11.9) * mm, "radius": 2.37 * mm});
            skPoint(sketch, "E16.1.1.37", {"position": v(-23.62, -23.62) * mm});
            skCircle(sketch, "E16.1.1.38", {"center": v(-27.65, -19.6) * mm, "radius": 2.37 * mm});
            skLineSegment(sketch, "E16.1.1.39", {"start": v(-31.5, 0) * mm, "end": v(-31.5, -15.75) * mm});
            skLineSegment(sketch, "E16.1.1.40", {"start": v(-1.47, -30.02) * mm, "end": v(-14.27, -30.02) * mm, "construction": true});
            skLineSegment(sketch, "E16.1.1.41", {"start": v(-14.27, -1.47) * mm, "end": v(-14.27, -14.27) * mm, "construction": true});
            skCircle(sketch, "E16.1.1.42", {"center": v(-3.85, -3.85) * mm, "radius": 2.37 * mm});
            skCircle(sketch, "E16.1.1.43", {"center": v(-11.9, -19.6) * mm, "radius": 2.37 * mm});
            skCircle(sketch, "E16.1.1.44", {"center": v(-27.65, -11.9) * mm, "radius": 2.37 * mm});
            skPoint(sketch, "E16.1.1.45", {"position": v(-7.87, -23.62) * mm});
            skLineSegment(sketch, "E16.1.1.46", {"start": v(-1.47, -14.27) * mm, "end": v(-14.27, -14.27) * mm, "construction": true});
            skLineSegment(sketch, "E16.1.1.47", {"start": v(-31.5, -31.5) * mm, "end": v(-15.75, -31.5) * mm, "construction": true});
            skCircle(sketch, "E16.1.1.48", {"center": v(-27.65, -3.85) * mm, "radius": 2.37 * mm});
            skLineSegment(sketch, "E16.1.1.49", {"start": v(-17.22, -1.47) * mm, "end": v(-30.02, -1.47) * mm, "construction": true});
            skLineSegment(sketch, "E16.1.1.50", {"start": v(-1.47, -17.22) * mm, "end": v(-1.47, -30.02) * mm, "construction": true});
            skCircle(sketch, "E16.1.1.51", {"center": v(-19.6, -27.65) * mm, "radius": 2.37 * mm});
            skLineSegment(sketch, "E16.1.1.52", {"start": v(-30.02, -23.62) * mm, "end": v(-17.22, -23.62) * mm, "construction": true});
            skLineSegment(sketch, "E16.1.1.53", {"start": v(-7.87, -1.47) * mm, "end": v(-7.87, -14.27) * mm, "construction": true});
            skLineSegment(sketch, "E16.1.1.54", {"start": v(0, 0) * mm, "end": v(-15.75, 0) * mm});
            skLineSegment(sketch, "E16.1.1.55", {"start": v(-23.62, -17.22) * mm, "end": v(-23.62, -30.02) * mm, "construction": true});
            skLineSegment(sketch, "E16.1.1.56", {"start": v(-1.47, -7.87) * mm, "end": v(-14.27, -7.87) * mm, "construction": true});
            skLineSegment(sketch, "E16.1.1.57", {"start": v(-31.5, -15.75) * mm, "end": v(-31.5, -31.5) * mm});
            skLineSegment(sketch, "E16.1.1.58", {"start": v(-15.75, -31.5) * mm, "end": v(-31.5, -31.5) * mm});
            skLineSegment(sketch, "E16.1.1.59", {"start": v(-30.02, -7.87) * mm, "end": v(-17.22, -7.87) * mm, "construction": true});
            skLineSegment(sketch, "E16.1.1.60", {"start": v(-15.75, 0) * mm, "end": v(-15.75, -15.75) * mm});
            skLineSegment(sketch, "E16.1.1.61", {"start": v(-1.47, -23.62) * mm, "end": v(-14.27, -23.62) * mm, "construction": true});
            skCircle(sketch, "E16.1.1.62", {"center": v(-11.9, -3.85) * mm, "radius": 2.37 * mm});
            skLineSegment(sketch, "E16.1.1.63", {"start": v(0, -15.75) * mm, "end": v(-15.75, -15.75) * mm});
            skCircle(sketch, "E16.1.1.64", {"center": v(-27.65, -19.6) * mm, "radius": 2.37 * mm});
            skPoint(sketch, "E16.1.1.65", {"position": v(-7.87, -23.62) * mm});
            skLineSegment(sketch, "E16.1.1.66", {"start": v(-15.75, -15.75) * mm, "end": v(-15.75, -31.5) * mm});
            skPoint(sketch, "E16.1.1.67", {"position": v(-23.62, -23.62) * mm});
            skLineSegment(sketch, "E16.1.1.68", {"start": v(-17.22, -23.62) * mm, "end": v(-30.02, -23.62) * mm, "construction": true});
            skPoint(sketch, "E16.1.1.69", {"position": v(-7.87, -7.87) * mm});
            skCircle(sketch, "E16.1.1.70", {"center": v(-11.9, -19.6) * mm, "radius": 2.37 * mm});
            skPoint(sketch, "E16.1.1.71", {"position": v(-23.62, -7.87) * mm});
            skLineSegment(sketch, "E16.1.1.72", {"start": v(-15.75, -15.75) * mm, "end": v(-31.5, -15.75) * mm});
            skCircle(sketch, "E16.1.1.73", {"center": v(-27.65, -3.85) * mm, "radius": 2.37 * mm});
            skLineSegment(sketch, "E16.1.1.74", {"start": v(-14.27, -7.87) * mm, "end": v(-1.47, -7.87) * mm, "construction": true});
            skLineSegment(sketch, "E16.1.1.75", {"start": v(-14.27, -23.62) * mm, "end": v(-1.47, -23.62) * mm, "construction": true});
            skLineSegment(sketch, "E16.1.1.76", {"start": v(-30.02, -23.62) * mm, "end": v(-17.22, -23.62) * mm, "construction": true});
            skLineSegment(sketch, "E16.1.1.77", {"start": v(-17.22, -7.87) * mm, "end": v(-30.02, -7.87) * mm, "construction": true});
            skLineSegment(sketch, "E16.direction1", {"start": v(0, 0) * mm, "end": v(-31.5, 0) * mm, "construction": true});
            skLineSegment(sketch, "E16.direction2", {"start": v(0, 0) * mm, "end": v(0, -31.5) * mm, "construction": true});
            skSolve(sketch);
        }
        {
            var Q0;
            Q0=makeQuery(id+"F6.imprint","IMPRINT",FACE,{"disambiguationData":[TD([[makeQuery(id+"F6.imprint","IMPRINT",EDGE,{"derivedFrom":sQuery(id+"F6.wireOp",EDGE,"E16.1.0.73")}),1.0]])]});
            var Q1;
            Q1=makeQuery(id+"F6.imprint","IMPRINT",FACE,{"disambiguationData":[TD([[makeQuery(id+"F6.imprint","IMPRINT",EDGE,{"derivedFrom":sQuery(id+"F6.wireOp",EDGE,"E16.1.0.22")}),-1.0]])]});
            var Q2;
            Q2=makeQuery(id+"F6.imprint","IMPRINT",FACE,{"disambiguationData":[TD([[makeQuery(id+"F6.imprint","IMPRINT",EDGE,{"derivedFrom":sQuery(id+"F6.wireOp",EDGE,"E16.1.0.62")}),1.0]])]});
            var Q3;
            Q3=makeQuery(id+"F6.imprint","IMPRINT",FACE,{"disambiguationData":[TD([[makeQuery(id+"F6.imprint","IMPRINT",EDGE,{"derivedFrom":sQuery(id+"F6.wireOp",EDGE,"E16.1.0.42")}),-1.0]])]});
            var Q4;
            Q4=makeQuery(id+"F6.imprint","IMPRINT",FACE,{"disambiguationData":[TD([[makeQuery(id+"F6.imprint","IMPRINT",EDGE,{"derivedFrom":sQuery(id+"F6.wireOp",EDGE,"E15.0.1.17")}),1.0]])]});
            var Q5;
            Q5=makeQuery(id+"F6.imprint","IMPRINT",FACE,{"disambiguationData":[TD([[makeQuery(id+"F6.imprint","IMPRINT",EDGE,{"derivedFrom":sQuery(id+"F6.wireOp",EDGE,"E15.0.1.8")}),-1.0]])]});
            var Q6;
            Q6=makeQuery(id+"F6.imprint","IMPRINT",FACE,{"disambiguationData":[TD([[makeQuery(id+"F6.imprint","IMPRINT",EDGE,{"derivedFrom":sQuery(id+"F6.wireOp",EDGE,"E15.1.1.17")}),1.0]])]});
            var Q7;
            Q7=makeQuery(id+"F6.imprint","IMPRINT",FACE,{"disambiguationData":[TD([[makeQuery(id+"F6.imprint","IMPRINT",EDGE,{"derivedFrom":sQuery(id+"F6.wireOp",EDGE,"E15.1.1.8")}),-1.0]])]});
            var Q8;
            Q8=makeQuery(id+"F6.imprint","IMPRINT",FACE,{"disambiguationData":[TD([[makeQuery(id+"F6.imprint","IMPRINT",EDGE,{"derivedFrom":sQuery(id+"F6.wireOp",EDGE,"E15.1.1.3")}),1.0]])]});
            var Q9;
            Q9=makeQuery(id+"F6.imprint","IMPRINT",FACE,{"disambiguationData":[TD([[makeQuery(id+"F6.imprint","IMPRINT",EDGE,{"derivedFrom":sQuery(id+"F6.wireOp",EDGE,"E15.1.1.5")}),-1.0]])]});
            var Q10;
            Q10=makeQuery(id+"F6.imprint","IMPRINT",FACE,{"disambiguationData":[TD([[makeQuery(id+"F6.imprint","IMPRINT",EDGE,{"derivedFrom":sQuery(id+"F6.wireOp",EDGE,"E15.0.1.3")}),1.0]])]});
            var Q11;
            Q11=makeQuery(id+"F6.imprint","IMPRINT",FACE,{"disambiguationData":[TD([[makeQuery(id+"F6.imprint","IMPRINT",EDGE,{"derivedFrom":sQuery(id+"F6.wireOp",EDGE,"E15.0.1.5")}),-1.0]])]});
            var Q12;
            Q12=makeQuery(id+"F6.imprint","IMPRINT",FACE,{"disambiguationData":[TD([[makeQuery(id+"F6.imprint","IMPRINT",EDGE,{"derivedFrom":sQuery(id+"F6.wireOp",EDGE,"E16.1.0.35")}),1.0]])]});
            var Q13;
            Q13=makeQuery(id+"F6.imprint","IMPRINT",FACE,{"disambiguationData":[TD([[makeQuery(id+"F6.imprint","IMPRINT",EDGE,{"derivedFrom":sQuery(id+"F6.wireOp",EDGE,"E16.1.0.9")}),-1.0]])]});
            var Q14;
            Q14=makeQuery(id+"F6.imprint","IMPRINT",FACE,{"disambiguationData":[TD([[makeQuery(id+"F6.imprint","IMPRINT",EDGE,{"derivedFrom":sQuery(id+"F6.wireOp",EDGE,"E16.1.0.36")}),1.0]])]});
            var Q15;
            Q15=makeQuery(id+"F6.imprint","IMPRINT",FACE,{"disambiguationData":[TD([[makeQuery(id+"F6.imprint","IMPRINT",EDGE,{"derivedFrom":sQuery(id+"F6.wireOp",EDGE,"E16.1.0.44")}),-1.0]])]});
            var Q16;
            Q16=makeQuery(id+"F6.imprint","IMPRINT",FACE,{"disambiguationData":[TD([[makeQuery(id+"F6.imprint","IMPRINT",EDGE,{"derivedFrom":sQuery(id+"F6.wireOp",EDGE,"E16.1.0.64")}),1.0]])]});
            var Q17;
            Q17=makeQuery(id+"F6.imprint","IMPRINT",FACE,{"disambiguationData":[TD([[makeQuery(id+"F6.imprint","IMPRINT",EDGE,{"derivedFrom":sQuery(id+"F6.wireOp",EDGE,"E16.1.0.7")}),-1.0]])]});
            var Q18;
            Q18=makeQuery(id+"F6.imprint","IMPRINT",FACE,{"disambiguationData":[TD([[makeQuery(id+"F6.imprint","IMPRINT",EDGE,{"derivedFrom":sQuery(id+"F6.wireOp",EDGE,"E16.1.0.70")}),1.0]])]});
            var Q19;
            Q19=makeQuery(id+"F6.imprint","IMPRINT",FACE,{"disambiguationData":[TD([[makeQuery(id+"F6.imprint","IMPRINT",EDGE,{"derivedFrom":sQuery(id+"F6.wireOp",EDGE,"E16.1.0.8")}),-1.0]])]});
            var Q20;
            Q20=makeQuery(id+"F6.imprint","IMPRINT",FACE,{"disambiguationData":[TD([[makeQuery(id+"F6.imprint","IMPRINT",EDGE,{"derivedFrom":sQuery(id+"F6.wireOp",EDGE,"E8")}),1.0]])]});
            var Q21;
            Q21=makeQuery(id+"F6.imprint","IMPRINT",FACE,{"disambiguationData":[TD([[makeQuery(id+"F6.imprint","IMPRINT",EDGE,{"derivedFrom":sQuery(id+"F6.wireOp",EDGE,"E12.MirrorC")}),-1.0]])]});
            var Q22;
            Q22=makeQuery(id+"F6.imprint","IMPRINT",FACE,{"disambiguationData":[TD([[makeQuery(id+"F6.imprint","IMPRINT",EDGE,{"derivedFrom":sQuery(id+"F6.wireOp",EDGE,"E15.1.0.17")}),1.0]])]});
            var Q23;
            Q23=makeQuery(id+"F6.imprint","IMPRINT",FACE,{"disambiguationData":[TD([[makeQuery(id+"F6.imprint","IMPRINT",EDGE,{"derivedFrom":sQuery(id+"F6.wireOp",EDGE,"E15.1.0.8")}),-1.0]])]});
            var Q24;
            Q24=makeQuery(id+"F6.imprint","IMPRINT",FACE,{"disambiguationData":[TD([[makeQuery(id+"F6.imprint","IMPRINT",EDGE,{"derivedFrom":sQuery(id+"F6.wireOp",EDGE,"E15.1.0.3")}),1.0]])]});
            var Q25;
            Q25=makeQuery(id+"F6.imprint","IMPRINT",FACE,{"disambiguationData":[TD([[makeQuery(id+"F6.imprint","IMPRINT",EDGE,{"derivedFrom":sQuery(id+"F6.wireOp",EDGE,"E15.1.0.5")}),-1.0]])]});
            var Q26;
            Q26=makeQuery(id+"F6.imprint","IMPRINT",FACE,{"disambiguationData":[TD([[makeQuery(id+"F6.imprint","IMPRINT",EDGE,{"derivedFrom":sQuery(id+"F6.wireOp",EDGE,"E14.MirrorC")}),1.0]])]});
            var Q27;
            Q27=makeQuery(id+"F6.imprint","IMPRINT",FACE,{"disambiguationData":[TD([[makeQuery(id+"F6.imprint","IMPRINT",EDGE,{"derivedFrom":sQuery(id+"F6.wireOp",EDGE,"E13.MirrorC")}),-1.0]])]});
            var Q28;
            Q28=makeQuery(id+"F6.imprint","IMPRINT",FACE,{"disambiguationData":[TD([[makeQuery(id+"F6.imprint","IMPRINT",EDGE,{"derivedFrom":sQuery(id+"F6.wireOp",EDGE,"E16.1.0.25")}),1.0]])]});
            var Q29;
            Q29=makeQuery(id+"F6.imprint","IMPRINT",FACE,{"disambiguationData":[TD([[makeQuery(id+"F6.imprint","IMPRINT",EDGE,{"derivedFrom":sQuery(id+"F6.wireOp",EDGE,"E16.1.0.16")}),-1.0]])]});
            var Q30;
            Q30=makeQuery(id+"F6.imprint","IMPRINT",FACE,{"disambiguationData":[TD([[makeQuery(id+"F6.imprint","IMPRINT",EDGE,{"derivedFrom":sQuery(id+"F6.wireOp",EDGE,"E16.1.0.51")}),1.0]])]});
            var Q31;
            Q31=makeQuery(id+"F6.imprint","IMPRINT",FACE,{"disambiguationData":[TD([[makeQuery(id+"F6.imprint","IMPRINT",EDGE,{"derivedFrom":sQuery(id+"F6.wireOp",EDGE,"E16.1.0.13")}),-1.0]])]});
            var Q32;
            Q32=makeQuery(id+"F6.imprint","IMPRINT",FACE,{"disambiguationData":[TD([[makeQuery(id+"F6.imprint","IMPRINT",EDGE,{"derivedFrom":sQuery(id+"F6.wireOp",EDGE,"E16.1.1.73")}),1.0]])]});
            var Q33;
            Q33=makeQuery(id+"F6.imprint","IMPRINT",FACE,{"disambiguationData":[TD([[makeQuery(id+"F6.imprint","IMPRINT",EDGE,{"derivedFrom":sQuery(id+"F6.wireOp",EDGE,"E16.1.1.22")}),-1.0]])]});
            var Q34;
            Q34=makeQuery(id+"F6.imprint","IMPRINT",FACE,{"disambiguationData":[TD([[makeQuery(id+"F6.imprint","IMPRINT",EDGE,{"derivedFrom":sQuery(id+"F6.wireOp",EDGE,"E16.1.1.62")}),1.0]])]});
            var Q35;
            Q35=makeQuery(id+"F6.imprint","IMPRINT",FACE,{"disambiguationData":[TD([[makeQuery(id+"F6.imprint","IMPRINT",EDGE,{"derivedFrom":sQuery(id+"F6.wireOp",EDGE,"E16.1.1.42")}),-1.0]])]});
            var Q36;
            Q36=makeQuery(id+"F6.imprint","IMPRINT",FACE,{"disambiguationData":[TD([[makeQuery(id+"F6.imprint","IMPRINT",EDGE,{"derivedFrom":sQuery(id+"F6.wireOp",EDGE,"E16.0.1.73")}),1.0]])]});
            var Q37;
            Q37=makeQuery(id+"F6.imprint","IMPRINT",FACE,{"disambiguationData":[TD([[makeQuery(id+"F6.imprint","IMPRINT",EDGE,{"derivedFrom":sQuery(id+"F6.wireOp",EDGE,"E16.0.1.22")}),-1.0]])]});
            var Q38;
            Q38=makeQuery(id+"F6.imprint","IMPRINT",FACE,{"disambiguationData":[TD([[makeQuery(id+"F6.imprint","IMPRINT",EDGE,{"derivedFrom":sQuery(id+"F6.wireOp",EDGE,"E16.0.1.62")}),1.0]])]});
            var Q39;
            Q39=makeQuery(id+"F6.imprint","IMPRINT",FACE,{"disambiguationData":[TD([[makeQuery(id+"F6.imprint","IMPRINT",EDGE,{"derivedFrom":sQuery(id+"F6.wireOp",EDGE,"E16.0.1.42")}),-1.0]])]});
            var Q40;
            Q40=makeQuery(id+"F6.imprint","IMPRINT",FACE,{"disambiguationData":[TD([[makeQuery(id+"F6.imprint","IMPRINT",EDGE,{"derivedFrom":sQuery(id+"F6.wireOp",EDGE,"E16.0.1.35")}),1.0]])]});
            var Q41;
            Q41=makeQuery(id+"F6.imprint","IMPRINT",FACE,{"disambiguationData":[TD([[makeQuery(id+"F6.imprint","IMPRINT",EDGE,{"derivedFrom":sQuery(id+"F6.wireOp",EDGE,"E16.0.1.9")}),-1.0]])]});
            var Q42;
            Q42=makeQuery(id+"F6.imprint","IMPRINT",FACE,{"disambiguationData":[TD([[makeQuery(id+"F6.imprint","IMPRINT",EDGE,{"derivedFrom":sQuery(id+"F6.wireOp",EDGE,"E16.0.1.36")}),1.0]])]});
            var Q43;
            Q43=makeQuery(id+"F6.imprint","IMPRINT",FACE,{"disambiguationData":[TD([[makeQuery(id+"F6.imprint","IMPRINT",EDGE,{"derivedFrom":sQuery(id+"F6.wireOp",EDGE,"E16.0.1.44")}),-1.0]])]});
            var Q44;
            Q44=makeQuery(id+"F6.imprint","IMPRINT",FACE,{"disambiguationData":[TD([[makeQuery(id+"F6.imprint","IMPRINT",EDGE,{"derivedFrom":sQuery(id+"F6.wireOp",EDGE,"E16.1.1.35")}),1.0]])]});
            var Q45;
            Q45=makeQuery(id+"F6.imprint","IMPRINT",FACE,{"disambiguationData":[TD([[makeQuery(id+"F6.imprint","IMPRINT",EDGE,{"derivedFrom":sQuery(id+"F6.wireOp",EDGE,"E16.1.1.9")}),-1.0]])]});
            var Q46;
            Q46=makeQuery(id+"F6.imprint","IMPRINT",FACE,{"disambiguationData":[TD([[makeQuery(id+"F6.imprint","IMPRINT",EDGE,{"derivedFrom":sQuery(id+"F6.wireOp",EDGE,"E16.1.1.36")}),1.0]])]});
            var Q47;
            Q47=makeQuery(id+"F6.imprint","IMPRINT",FACE,{"disambiguationData":[TD([[makeQuery(id+"F6.imprint","IMPRINT",EDGE,{"derivedFrom":sQuery(id+"F6.wireOp",EDGE,"E16.1.1.44")}),-1.0]])]});
            var Q48;
            Q48=makeQuery(id+"F6.imprint","IMPRINT",FACE,{"disambiguationData":[TD([[makeQuery(id+"F6.imprint","IMPRINT",EDGE,{"derivedFrom":sQuery(id+"F6.wireOp",EDGE,"E16.1.1.64")}),1.0]])]});
            var Q49;
            Q49=makeQuery(id+"F6.imprint","IMPRINT",FACE,{"disambiguationData":[TD([[makeQuery(id+"F6.imprint","IMPRINT",EDGE,{"derivedFrom":sQuery(id+"F6.wireOp",EDGE,"E16.1.1.7")}),-1.0]])]});
            var Q50;
            Q50=makeQuery(id+"F6.imprint","IMPRINT",FACE,{"disambiguationData":[TD([[makeQuery(id+"F6.imprint","IMPRINT",EDGE,{"derivedFrom":sQuery(id+"F6.wireOp",EDGE,"E16.1.1.70")}),1.0]])]});
            var Q51;
            Q51=makeQuery(id+"F6.imprint","IMPRINT",FACE,{"disambiguationData":[TD([[makeQuery(id+"F6.imprint","IMPRINT",EDGE,{"derivedFrom":sQuery(id+"F6.wireOp",EDGE,"E16.1.1.8")}),-1.0]])]});
            var Q52;
            Q52=makeQuery(id+"F6.imprint","IMPRINT",FACE,{"disambiguationData":[TD([[makeQuery(id+"F6.imprint","IMPRINT",EDGE,{"derivedFrom":sQuery(id+"F6.wireOp",EDGE,"E16.0.1.64")}),1.0]])]});
            var Q53;
            Q53=makeQuery(id+"F6.imprint","IMPRINT",FACE,{"disambiguationData":[TD([[makeQuery(id+"F6.imprint","IMPRINT",EDGE,{"derivedFrom":sQuery(id+"F6.wireOp",EDGE,"E16.0.1.7")}),-1.0]])]});
            var Q54;
            Q54=makeQuery(id+"F6.imprint","IMPRINT",FACE,{"disambiguationData":[TD([[makeQuery(id+"F6.imprint","IMPRINT",EDGE,{"derivedFrom":sQuery(id+"F6.wireOp",EDGE,"E16.0.1.70")}),1.0]])]});
            var Q55;
            Q55=makeQuery(id+"F6.imprint","IMPRINT",FACE,{"disambiguationData":[TD([[makeQuery(id+"F6.imprint","IMPRINT",EDGE,{"derivedFrom":sQuery(id+"F6.wireOp",EDGE,"E16.0.1.8")}),-1.0]])]});
            var Q56;
            Q56=makeQuery(id+"F6.imprint","IMPRINT",FACE,{"disambiguationData":[TD([[makeQuery(id+"F6.imprint","IMPRINT",EDGE,{"derivedFrom":sQuery(id+"F6.wireOp",EDGE,"E16.0.1.25")}),1.0]])]});
            var Q57;
            Q57=makeQuery(id+"F6.imprint","IMPRINT",FACE,{"disambiguationData":[TD([[makeQuery(id+"F6.imprint","IMPRINT",EDGE,{"derivedFrom":sQuery(id+"F6.wireOp",EDGE,"E16.0.1.16")}),-1.0]])]});
            var Q58;
            Q58=makeQuery(id+"F6.imprint","IMPRINT",FACE,{"disambiguationData":[TD([[makeQuery(id+"F6.imprint","IMPRINT",EDGE,{"derivedFrom":sQuery(id+"F6.wireOp",EDGE,"E16.0.1.51")}),1.0]])]});
            var Q59;
            Q59=makeQuery(id+"F6.imprint","IMPRINT",FACE,{"disambiguationData":[TD([[makeQuery(id+"F6.imprint","IMPRINT",EDGE,{"derivedFrom":sQuery(id+"F6.wireOp",EDGE,"E16.0.1.13")}),-1.0]])]});
            var Q60;
            Q60=makeQuery(id+"F6.imprint","IMPRINT",FACE,{"disambiguationData":[TD([[makeQuery(id+"F6.imprint","IMPRINT",EDGE,{"derivedFrom":sQuery(id+"F6.wireOp",EDGE,"E16.1.1.25")}),1.0]])]});
            var Q61;
            Q61=makeQuery(id+"F6.imprint","IMPRINT",FACE,{"disambiguationData":[TD([[makeQuery(id+"F6.imprint","IMPRINT",EDGE,{"derivedFrom":sQuery(id+"F6.wireOp",EDGE,"E16.1.1.16")}),-1.0]])]});
            var Q62;
            Q62=makeQuery(id+"F6.imprint","IMPRINT",FACE,{"disambiguationData":[TD([[makeQuery(id+"F6.imprint","IMPRINT",EDGE,{"derivedFrom":sQuery(id+"F6.wireOp",EDGE,"E16.1.1.51")}),1.0]])]});
            var Q63;
            Q63=makeQuery(id+"F6.imprint","IMPRINT",FACE,{"disambiguationData":[TD([[makeQuery(id+"F6.imprint","IMPRINT",EDGE,{"derivedFrom":sQuery(id+"F6.wireOp",EDGE,"E16.1.1.13")}),-1.0]])]});
            extrude(context, id + "F7", {"entities" : qUnion([Q0, Q1, Q2, Q3, Q4, Q5, Q6, Q7, Q8, Q9, Q10, Q11, Q12, Q13, Q14, Q15, Q16, Q17, Q18, Q19, Q20, Q21, Q22, Q23, Q24, Q25, Q26, Q27, Q28, Q29, Q30, Q31, Q32, Q33, Q34, Q35, Q36, Q37, Q38, Q39, Q40, Q41, Q42, Q43, Q44, Q45, Q46, Q47, Q48, Q49, Q50, Q51, Q52, Q53, Q54, Q55, Q56, Q57, Q58, Q59, Q60, Q61, Q62, Q63]), "operationType" : NewBodyOperationType.ADD, "depth" : 1.83 * mm, "offsetDistance" : 25.4 * mm});
        }
    });
